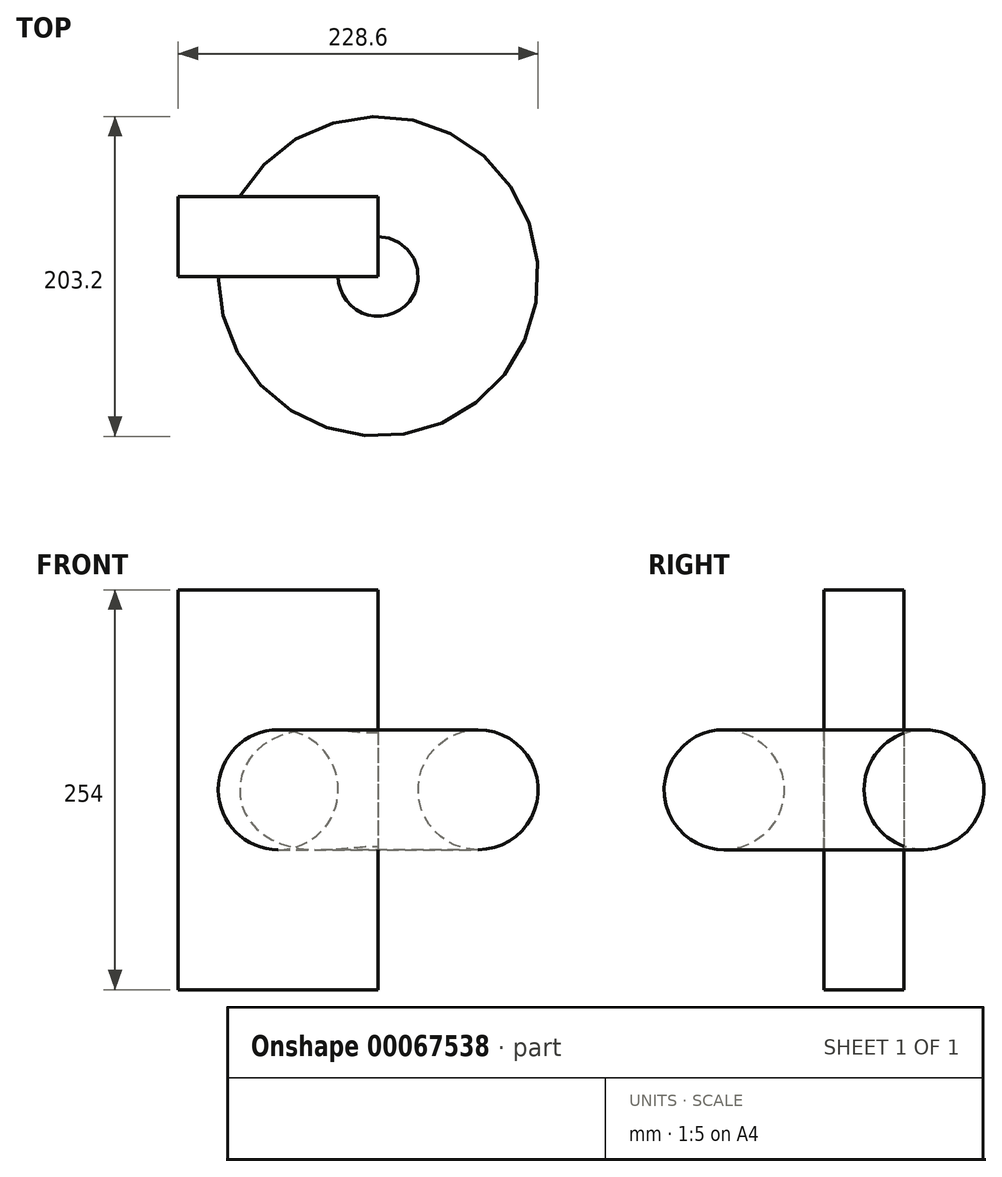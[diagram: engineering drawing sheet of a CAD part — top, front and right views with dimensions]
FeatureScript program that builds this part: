
annotation { "Feature Type Name" : "Feature", "Feature Type Description" : "" }
export const myFeature = defineFeature(function(context is Context, id is Id, definition is map)
    precondition{}
    {
        {
            var Q0;
            Q0=qCreatedBy(makeId("Front.planeOp"),FACE);
            var sketch = newSketch(context, id + "F0", { "sketchPlane" : qUnion([Q0])});
            skLineSegment(sketch, "E0.bottom", {"start": v(-63.5, 127) * mm, "end": v(63.5, 127) * mm});
            skLineSegment(sketch, "E0.top", {"start": v(-63.5, -127) * mm, "end": v(63.5, -127) * mm});
            skLineSegment(sketch, "E0.left", {"start": v(-63.5, 127) * mm, "end": v(-63.5, -127) * mm});
            skLineSegment(sketch, "E0.right", {"start": v(63.5, 127) * mm, "end": v(63.5, -127) * mm});
            skPoint(sketch, "E0.middle", {"position": v(0, 0) * mm});
            skSolve(sketch);
        }
        {
            var Q0;
            Q0 = qSketchRegion(id + "F0", true);
            extrude(context, id + "F1", {"entities" : qUnion([Q0]), "depth" : 50.8 * mm, "offsetDistance" : 25.4 * mm});
        }
        {
            var Q0;
            Q0=makeQuery(id+"F1.opExtrude","CAP_FACE",FACE,{"disambiguationData":[OSD([sQuery(id+"F0.wireOp",EDGE,"E0.bottom"),sQuery(id+"F0.wireOp",EDGE,"E0.top"),sQuery(id+"F0.wireOp",EDGE,"E0.left"),sQuery(id+"F0.wireOp",EDGE,"E0.right")])],"isStart":false});
            var sketch = newSketch(context, id + "F2", { "sketchPlane" : qUnion([Q0])});
            skCircle(sketch, "E1", {"center": v(0, 0) * mm, "radius": 38.1 * mm});
            skSolve(sketch);
        }
        {
            var Q0;
            Q0 = qSketchRegion(id + "F2", true);
            var Q1;
            Q1=makeQuery(id+"F1.opExtrude","CAP_EDGE",EDGE,{"disambiguationData":[OSD([sQuery(id+"F0.wireOp",EDGE,"E0.right")])],"isStart":false});
            revolve(context, id + "F3", {"operationType" : NewBodyOperationType.ADD, "surfaceOperationType" : NewSurfaceOperationType.NEW, "entities" : qUnion([Q0]), "axis" : qUnion([Q1]), "revolveType" : RevolveType.FULL});
        }
    });
